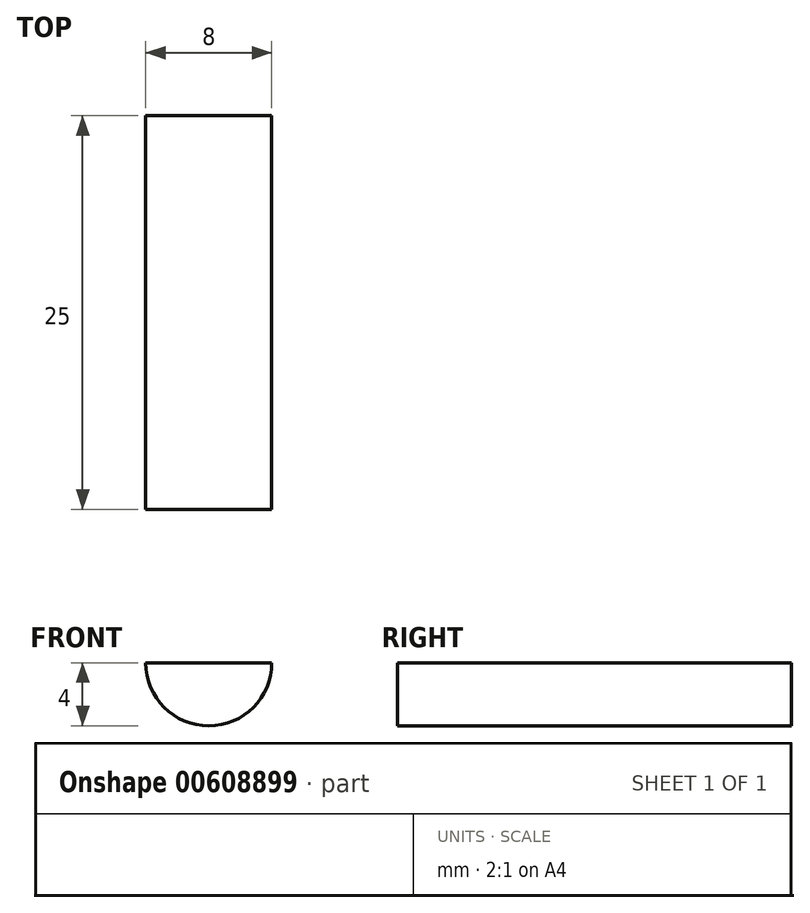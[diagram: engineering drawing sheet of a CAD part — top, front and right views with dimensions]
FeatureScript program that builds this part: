
annotation { "Feature Type Name" : "Feature", "Feature Type Description" : "" }
export const myFeature = defineFeature(function(context is Context, id is Id, definition is map)
    precondition{}
    {
        {
            var Q0;
            Q0=qCreatedBy(makeId("Front.planeOp"),FACE);
            var sketch = newSketch(context, id + "F0", { "sketchPlane" : qUnion([Q0])});
            skLineSegment(sketch, "E0", {"start": v(0, 0) * mm, "end": v(12.5, 0) * mm});
            skLineSegment(sketch, "E1", {"start": v(12.5, 0) * mm, "end": v(5, 25) * mm});
            skLineSegment(sketch, "E2", {"start": v(5, 25) * mm, "end": v(5, 80) * mm});
            skLineSegment(sketch, "E3", {"start": v(5, 80) * mm, "end": v(0, 80) * mm});
            skLineSegment(sketch, "E4", {"start": v(0, 80) * mm, "end": v(0, 0) * mm});
            skSolve(sketch);
        }
        {
            var Q0;
            Q0=makeQuery(id+"F0.imprint","IMPRINT",FACE,{"disambiguationData":[TD([[makeQuery(id+"F0.imprint","IMPRINT",EDGE,{"derivedFrom":sQuery(id+"F0.wireOp",EDGE,"E0")}),1.0]])]});
            extrude(context, id + "F1", {"entities" : qUnion([Q0]), "depth" : 25 * mm, "offsetDistance" : 25 * mm});
        }
        {
            var Q0;
            Q0=makeQuery(id+"F1.opExtrude","SWEPT_FACE",FACE,{"disambiguationData":[OSD([sQuery(id+"F0.wireOp",EDGE,"E4")])]});
            var sketch = newSketch(context, id + "F2", { "sketchPlane" : qUnion([Q0])});
            skArc(sketch, "E5", {"start": v(16.5, 0) * mm, "mid": v(12.5, 4) * mm, "end": v(8.5, 0) * mm});
            skSolve(sketch);
        }
        {
            var Q0;
            Q0=makeQuery(id+"F1.opExtrude","CAP_FACE",FACE,{"disambiguationData":[OSD([sQuery(id+"F0.wireOp",EDGE,"E0"),sQuery(id+"F0.wireOp",EDGE,"E1"),sQuery(id+"F0.wireOp",EDGE,"E2"),sQuery(id+"F0.wireOp",EDGE,"E3"),sQuery(id+"F0.wireOp",EDGE,"E4")])],"isStart":false});
            var sketch = newSketch(context, id + "F3", { "sketchPlane" : qUnion([Q0])});
            skArc(sketch, "E6", {"start": v(4, 80) * mm, "mid": v(2.83, 77.17) * mm, "end": v(0, 76) * mm});
            skSolve(sketch);
        }
        {
            var Q0;
            {var subQ0=sQuery(id+"F3.wireOp",EDGE,"E6");Q0=makeQuery(id+"F3.imprint","IMPRINT",FACE,{"disambiguationData":[TD([[makeQuery(id+"F3.imprint","IMPRINT",EDGE,{"derivedFrom":subQ0}),-1.0]])]});}
            extrude(context, id + "F4", {"entities" : qUnion([Q0]), "operationType" : NewBodyOperationType.REMOVE, "oppositeDirection" : true, "depth" : 30 * mm, "offsetDistance" : 25 * mm});
        }
        {
            var Q0;
            {var subQ0=sQuery(id+"F2.wireOp",EDGE,"E5");Q0=makeQuery(id+"F2.imprint","IMPRINT",FACE,{"disambiguationData":[TD([[makeQuery(id+"F2.imprint","IMPRINT",EDGE,{"derivedFrom":subQ0}),1.0]])]});}
            extrude(context, id + "F5", {"entities" : qUnion([Q0]), "operationType" : NewBodyOperationType.REMOVE, "oppositeDirection" : true, "depth" : 15 * mm, "offsetDistance" : 25 * mm});
        }
        {
            var Q0;
            Q0=makeQuery(id+"F1.opExtrude","SWEPT_BODY",BODY,{"disambiguationData":[OSD([sQuery(id+"F0.wireOp",EDGE,"E0"),sQuery(id+"F0.wireOp",EDGE,"E1"),sQuery(id+"F0.wireOp",EDGE,"E2"),sQuery(id+"F0.wireOp",EDGE,"E3"),sQuery(id+"F0.wireOp",EDGE,"E4")])]});
            var Q1;
            Q1=qCreatedBy(makeId("Right.planeOp"),FACE);
            mirror(context, id + "F6", {"operationType" : NewBodyOperationType.ADD, "entities" : qUnion([Q0]), "mirrorPlane" : qUnion([Q1])});
        }
    });
